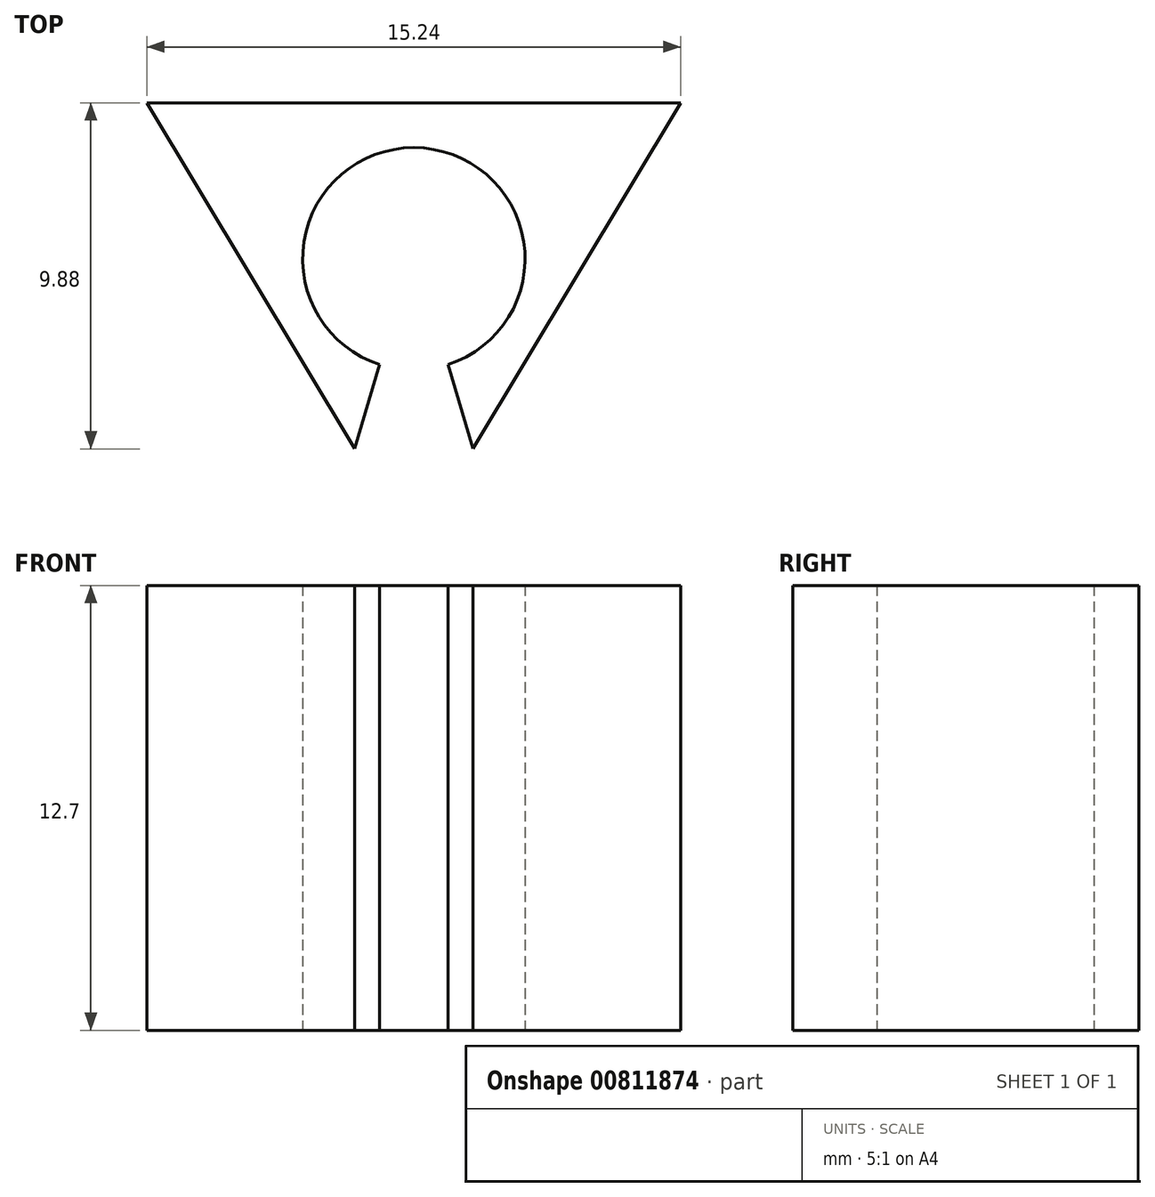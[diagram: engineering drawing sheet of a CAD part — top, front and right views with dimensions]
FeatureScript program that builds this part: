
annotation { "Feature Type Name" : "Feature", "Feature Type Description" : "" }
export const myFeature = defineFeature(function(context is Context, id is Id, definition is map)
    precondition{}
    {
        {
            var Q0;
            Q0=qCreatedBy(makeId("Top.planeOp"),FACE);
            var sketch = newSketch(context, id + "F0", { "sketchPlane" : qUnion([Q0])});
            skLineSegment(sketch, "E0", {"start": v(0, 0) * mm, "end": v(7.62, 0) * mm});
            skLineSegment(sketch, "E1", {"start": v(0, 0) * mm, "end": v(-7.62, 0) * mm});
            skLineSegment(sketch, "E2", {"start": v(0, -10.16) * mm, "end": v(1.52, -10.16) * mm});
            skLineSegment(sketch, "E3", {"start": v(0, -10.16) * mm, "end": v(-1.52, -10.16) * mm});
            skLineSegment(sketch, "E4", {"start": v(7.62, 0) * mm, "end": v(1.52, -10.16) * mm});
            skLineSegment(sketch, "E5", {"start": v(-7.62, 0) * mm, "end": v(-1.52, -10.16) * mm});
            skLineSegment(sketch, "E6", {"start": v(0, 0) * mm, "end": v(0, -10.16) * mm});
            skSolve(sketch);
        }
        {
            var Q0;
            Q0=makeQuery(id+"F0.imprint","IMPRINT",FACE,{"disambiguationData":[TD([[makeQuery(id+"F0.imprint","IMPRINT",EDGE,{"derivedFrom":sQuery(id+"F0.wireOp",EDGE,"E0")}),-1.0]])]});
            var sketch = newSketch(context, id + "F1", { "sketchPlane" : qUnion([Q0])});
            skCircle(sketch, "E7", {"center": v(0, -4.46) * mm, "radius": 3.17 * mm});
            skSolve(sketch);
        }
        {
            var Q0;
            Q0=makeQuery(id+"F0.imprint","IMPRINT",FACE,{"disambiguationData":[TD([[makeQuery(id+"F0.imprint","IMPRINT",EDGE,{"derivedFrom":sQuery(id+"F0.wireOp",EDGE,"E0")}),-1.0]])]});
            var sketch = newSketch(context, id + "F2", { "sketchPlane" : qUnion([Q0])});
            skLineSegment(sketch, "E8", {"start": v(0, -7.62) * mm, "end": v(1.02, -7.62) * mm});
            skLineSegment(sketch, "E9", {"start": v(0, -7.62) * mm, "end": v(-1.02, -7.62) * mm});
            skLineSegment(sketch, "E10", {"start": v(0, -7.62) * mm, "end": v(0, -5.08) * mm});
            skLineSegment(sketch, "E11", {"start": v(0.25, -5.05) * mm, "end": v(1.02, -7.62) * mm});
            skLineSegment(sketch, "E12", {"start": v(-0.25, -5.05) * mm, "end": v(-1.02, -7.62) * mm});
            skLineSegment(sketch, "E13", {"start": v(0, -5.08) * mm, "end": v(0.25, -5.08) * mm});
            skLineSegment(sketch, "E14", {"start": v(0, -5.08) * mm, "end": v(-0.25, -5.08) * mm});
            skLineSegment(sketch, "E15", {"start": v(0.25, -5.08) * mm, "end": v(2.08, -11.16) * mm});
            skLineSegment(sketch, "E16", {"start": v(-0.25, -5.08) * mm, "end": v(-2.08, -11.16) * mm});
            skLineSegment(sketch, "E17", {"start": v(2.08, -11.16) * mm, "end": v(-2.08, -11.16) * mm});
            skSolve(sketch);
        }
        {
            var Q0;
            Q0 = qSketchRegion(id + "F0", true);
            extrude(context, id + "F3", {"entities" : qUnion([Q0]), "depth" : 12.7 * mm, "offsetDistance" : 25.4 * mm});
        }
        {
            var Q0;
            Q0 = qSketchRegion(id + "F2", true);
            extrude(context, id + "F4", {"entities" : qUnion([Q0]), "operationType" : NewBodyOperationType.REMOVE, "oppositeDirection" : true, "depth" : -12.7 * mm, "offsetDistance" : 25.4 * mm});
        }
        {
            var Q0;
            Q0 = qSketchRegion(id + "F1", true);
            extrude(context, id + "F5", {"entities" : qUnion([Q0]), "operationType" : NewBodyOperationType.REMOVE, "oppositeDirection" : true, "depth" : -12.7 * mm, "offsetDistance" : 25.4 * mm});
        }
    });
